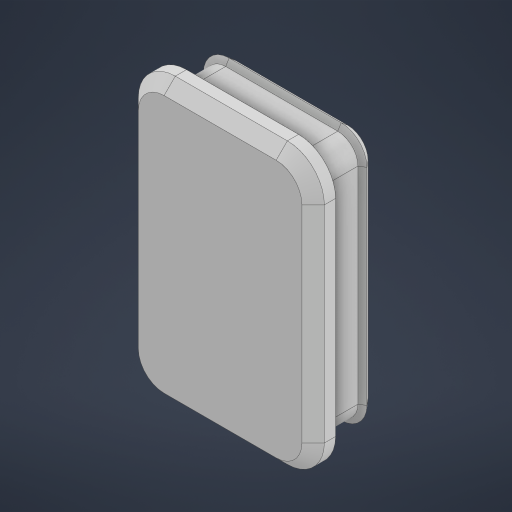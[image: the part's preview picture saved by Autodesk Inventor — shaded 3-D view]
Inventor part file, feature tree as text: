
AUTODESK INVENTOR PART (.ipt)
format: ipt  version: 2023 (Build 270158000, 158)  size: 257,024 bytes
history: native  units: in
note: dims shown in document units (in); Inventor stores cm internally (conversion verified against a paired STEP export)
features: extrude x3, chamfer x3, sketch x1
ambient origin geometry x8: Origin, YZ Plane, XZ Plane, XY Plane, X Axis, Y Axis, Z Axis, Center Point
bodies: Solid1 (feature_tree)
feature tree (7):
  sketch  "Sketch1"  dims[d0=0.2756in d1=0.4409in d2=0.0394in d3=0.0256in d4=0.0394in d5=0.0in d6=0.0039in d7=0.0866in d8=0.0in d9=0.0276in d10=0.0059in d11=0.0689in d12=0.0in d14=0.0098in d15=0.0059in d16=45.0deg d17=0.0197in d18=0.0197in d19=45.0deg d20=0.0098in d21=0.0118in d22=45.0deg]
  extrude  "Extrusion1"  Depth=0.0276in
  extrude  "Extrusion2"  Depth=0.0394in
  extrude  "Extrusion3"  Depth=0.0276in
  chamfer  "Chamfer1"  Distance=0.0394in
  chamfer  "Chamfer2"  Distance=0.0039in
  chamfer  "Chamfer3"  Distance=0.0866in
